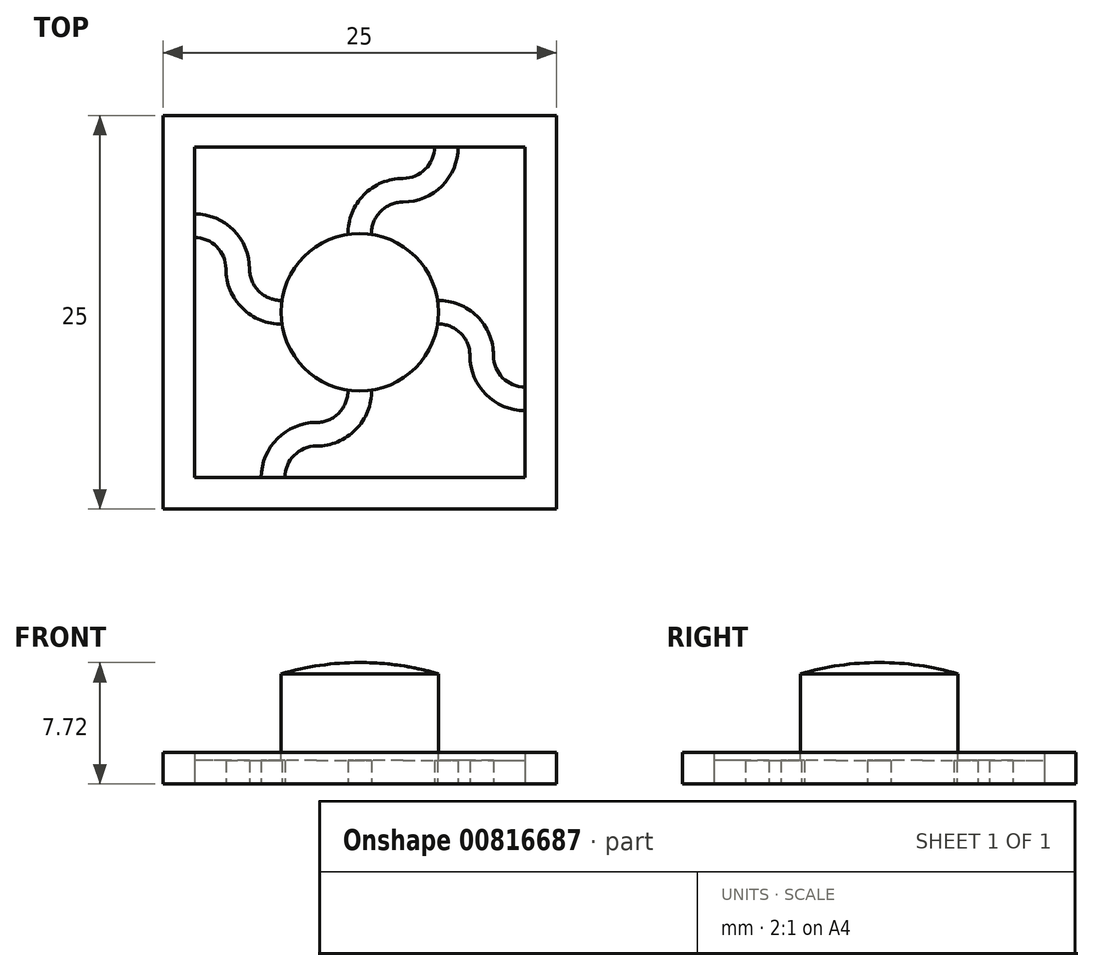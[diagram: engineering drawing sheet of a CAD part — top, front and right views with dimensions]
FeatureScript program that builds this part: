
annotation { "Feature Type Name" : "Feature", "Feature Type Description" : "" }
export const myFeature = defineFeature(function(context is Context, id is Id, definition is map)
    precondition{}
    {
        {
            var Q0;
            Q0=qCreatedBy(makeId("Top.planeOp"),FACE);
            var sketch = newSketch(context, id + "F0", { "sketchPlane" : qUnion([Q0])});
            skCircle(sketch, "E0", {"center": v(0, 0) * mm, "radius": 4.84 * mm});
            skPoint(sketch, "E1", {"position": v(2.75, 5) * mm});
            skPoint(sketch, "E2", {"position": v(2.75, 7) * mm});
            skPoint(sketch, "E3", {"position": v(2.75, 8.5) * mm});
            skArc(sketch, "E4", {"start": v(2.75, 7) * mm, "mid": v(1.26, 6.33) * mm, "end": v(0.76, 4.78) * mm});
            skArc(sketch, "E5", {"start": v(2.75, 8.5) * mm, "mid": v(0.2, 7.4) * mm, "end": v(-0.74, 4.78) * mm});
            skPoint(sketch, "E6", {"position": v(2.75, 10.5) * mm});
            skArc(sketch, "E7", {"start": v(2.75, 7) * mm, "mid": v(5.22, 8.03) * mm, "end": v(6.25, 10.5) * mm});
            skArc(sketch, "E8", {"start": v(2.75, 8.5) * mm, "mid": v(4.16, 9.09) * mm, "end": v(4.75, 10.5) * mm});
            skPoint(sketch, "E9", {"position": v(0, 21) * mm});
            skArc(sketch, "E10.1.0", {"start": v(-8.5, 2.75) * mm, "mid": v(-7.4, 0.2) * mm, "end": v(-4.78, -0.74) * mm});
            skArc(sketch, "E10.1.1", {"start": v(-7, 2.75) * mm, "mid": v(-6.33, 1.26) * mm, "end": v(-4.78, 0.76) * mm});
            skArc(sketch, "E10.1.2", {"start": v(-7, 2.75) * mm, "mid": v(-8.03, 5.22) * mm, "end": v(-10.5, 6.25) * mm});
            skArc(sketch, "E10.1.3", {"start": v(-8.5, 2.75) * mm, "mid": v(-9.09, 4.16) * mm, "end": v(-10.5, 4.75) * mm});
            skArc(sketch, "E10.2.0", {"start": v(-2.75, -8.5) * mm, "mid": v(-0.2, -7.4) * mm, "end": v(0.74, -4.78) * mm});
            skArc(sketch, "E10.2.1", {"start": v(-2.75, -7) * mm, "mid": v(-1.26, -6.33) * mm, "end": v(-0.76, -4.78) * mm});
            skArc(sketch, "E10.2.2", {"start": v(-2.75, -7) * mm, "mid": v(-5.22, -8.03) * mm, "end": v(-6.25, -10.5) * mm});
            skArc(sketch, "E10.2.3", {"start": v(-2.75, -8.5) * mm, "mid": v(-4.16, -9.09) * mm, "end": v(-4.75, -10.5) * mm});
            skArc(sketch, "E10.3.0", {"start": v(8.5, -2.75) * mm, "mid": v(7.4, -0.2) * mm, "end": v(4.78, 0.74) * mm});
            skArc(sketch, "E10.3.1", {"start": v(7, -2.75) * mm, "mid": v(6.33, -1.26) * mm, "end": v(4.78, -0.76) * mm});
            skArc(sketch, "E10.3.2", {"start": v(7, -2.75) * mm, "mid": v(8.03, -5.22) * mm, "end": v(10.5, -6.25) * mm});
            skArc(sketch, "E10.3.3", {"start": v(8.5, -2.75) * mm, "mid": v(9.09, -4.16) * mm, "end": v(10.5, -4.75) * mm});
            skLineSegment(sketch, "E11", {"start": v(-10.5, 10.5) * mm, "end": v(10.5, 10.5) * mm});
            skLineSegment(sketch, "E12", {"start": v(10.5, 10.5) * mm, "end": v(10.5, -10.5) * mm});
            skLineSegment(sketch, "E13", {"start": v(10.5, -10.5) * mm, "end": v(-10.5, -10.5) * mm});
            skLineSegment(sketch, "E14", {"start": v(-10.5, -10.5) * mm, "end": v(-10.5, 10.5) * mm});
            skLineSegment(sketch, "E15", {"start": v(-12.5, 12.5) * mm, "end": v(12.5, 12.5) * mm});
            skLineSegment(sketch, "E16", {"start": v(12.5, 12.5) * mm, "end": v(12.5, -12.5) * mm});
            skLineSegment(sketch, "E17", {"start": v(-12.5, 12.5) * mm, "end": v(-12.5, -12.5) * mm});
            skLineSegment(sketch, "E18", {"start": v(-12.5, -12.5) * mm, "end": v(12.5, -12.5) * mm});
            skSolve(sketch);
        }
        {
            var Q0;
            Q0=qCreatedBy(makeId("Front.planeOp"),FACE);
            var sketch = newSketch(context, id + "F1", { "sketchPlane" : qUnion([Q0])});
            skLineSegment(sketch, "E19", {"start": v(0, 0) * mm, "end": v(-5, 0) * mm});
            skLineSegment(sketch, "E20", {"start": v(-5, 0) * mm, "end": v(-5, 7) * mm});
            skArc(sketch, "E21", {"start": v(-5, 7) * mm, "mid": v(-2.53, 7.54) * mm, "end": v(0, 7.72) * mm});
            skLineSegment(sketch, "E22", {"start": v(0, 7.72) * mm, "end": v(0, 0) * mm});
            skSolve(sketch);
        }
        {
            var Q0;
            Q0=makeQuery(id+"F1.imprint","IMPRINT",FACE,{"disambiguationData":[TD([[makeQuery(id+"F1.imprint","IMPRINT",EDGE,{"derivedFrom":sQuery(id+"F1.wireOp",EDGE,"E19")}),-1.0]])]});
            var Q1;
            Q1=sQuery(id+"F1.wireOp",EDGE,"E22");
            revolve(context, id + "F2", {"surfaceOperationType" : NewSurfaceOperationType.NEW, "entities" : qUnion([Q0]), "axis" : qUnion([Q1]), "revolveType" : RevolveType.FULL});
        }
        {
            var Q0;
            {var subQ1=sQuery(id+"F0.wireOp",EDGE,"E10.1.0");Q0=makeQuery(id+"F0.imprint","IMPRINT",FACE,{"disambiguationData":[TD([[makeQuery(id+"F0.imprint","IMPRINT",EDGE,{"derivedFrom":subQ1}),1.0]])]});}
            var Q1;
            {var subQ1=sQuery(id+"F0.wireOp",EDGE,"E10.3.0");Q1=makeQuery(id+"F0.imprint","IMPRINT",FACE,{"disambiguationData":[TD([[makeQuery(id+"F0.imprint","IMPRINT",EDGE,{"derivedFrom":subQ1}),1.0]])]});}
            var Q2;
            {var subQ1=sQuery(id+"F0.wireOp",EDGE,"E4");Q2=makeQuery(id+"F0.imprint","IMPRINT",FACE,{"disambiguationData":[TD([[makeQuery(id+"F0.imprint","IMPRINT",EDGE,{"derivedFrom":subQ1}),-1.0]])]});}
            var Q3;
            {var subQ6=sQuery(id+"F0.wireOp",EDGE,"E10.2.0");Q3=makeQuery(id+"F0.imprint","IMPRINT",FACE,{"disambiguationData":[TD([[makeQuery(id+"F0.imprint","IMPRINT",EDGE,{"derivedFrom":subQ6}),1.0]])]});}
            extrude(context, id + "F3", {"entities" : qUnion([Q0, Q1, Q2, Q3]), "operationType" : NewBodyOperationType.ADD, "depth" : 1.5 * mm, "offsetDistance" : 25 * mm});
        }
        {
            var Q0;
            Q0=makeQuery(id+"F0.imprint","IMPRINT",FACE,{"disambiguationData":[TD([[makeQuery(id+"F0.imprint","IMPRINT",EDGE,{"derivedFrom":sQuery(id+"F0.wireOp",EDGE,"E15")}),-1.0]])]});
            extrude(context, id + "F4", {"entities" : qUnion([Q0]), "operationType" : NewBodyOperationType.ADD, "depth" : 2 * mm, "offsetDistance" : 25 * mm});
        }
    });
